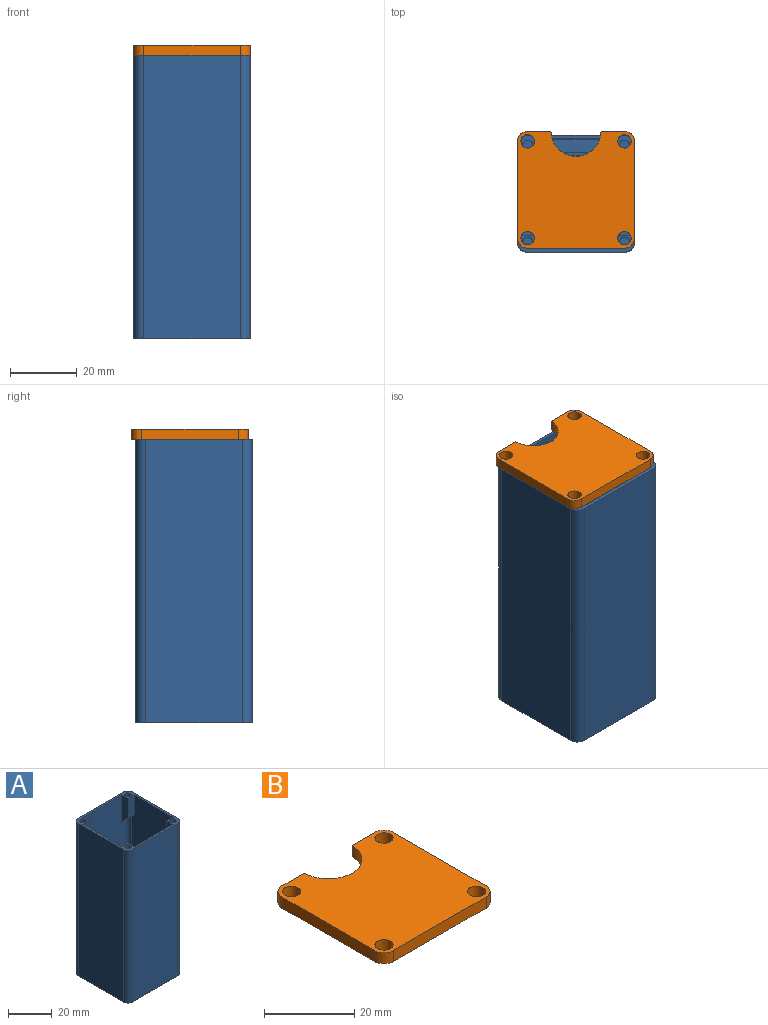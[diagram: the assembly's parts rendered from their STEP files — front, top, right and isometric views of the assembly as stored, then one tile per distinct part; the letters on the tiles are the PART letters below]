
ASSEMBLY  parts=2 mates=1
PART A: 41 faces, bbox 39.3x39.3x85.6 mm
  f0: plane 81x29mm, normal (0,-1,0), area 2289mm2, adj f4,f11,f22,f31,f35,f36,f37,f39
  f1: plane 81x29mm, normal (0,1,0), area 2289mm2, adj f4,f11,f25,f28,f33,f34,f38,f40
  f2: plane 81x29mm, normal (-1,0,0), area 2301mm2, adj f4,f11,f27,f30,f34,f36,f37,f38
  f3: plane 81x29mm, normal (1,0,0), area 2301mm2, adj f4,f11,f21,f24,f33,f35,f39,f40
  f4: plane 33x33mm, normal (0,0,1), area 460.6mm2, adj f0,f1,f2,f3,f16,f17,f18,f19
  f5: torus R=15mm, axis (0,0,1), area 344.5mm2, adj f10,f20
  f6: plane 85x29mm, normal (0,-1,0), area 2465mm2, adj f10,f11,f12,f15
  f7: plane 85x29mm, normal (1,0,0), area 2465mm2, adj f10,f11,f12,f13
  f8: plane 85x29mm, normal (0,1,0), area 2465mm2, adj f10,f11,f13,f14
  f9: plane 85x29mm, normal (-1,0,0), area 2465mm2, adj f10,f11,f14,f15
  f10: plane 35x35mm, normal (0,0,-1), area 510.4mm2, adj f5,f6,f7,f8,f9,f12,f13,f14
  f11: plane 35x35mm, normal (0,0,1), area 164mm2, adj f0,f1,f2,f3,f6,f7,f8,f9
  f12: cylinder r=3mm len=85mm, axis (0,0,1), area 400.6mm2, adj f6,f7,f10,f11
  f13: cylinder r=3mm len=85mm, axis (0,0,-1), area 400.6mm2, adj f7,f8,f10,f11
  f14: cylinder r=3mm len=85mm, axis (0,0,1), area 400.6mm2, adj f8,f9,f10,f11
  f15: cylinder r=3mm len=85mm, axis (0,0,-1), area 400.6mm2, adj f6,f9,f10,f11
  f16: plane 25x2mm, normal (0,1,0), area 50mm2, adj f4,f17,f19,f20
  f17: plane 25x2mm, normal (-1,0,0), area 50mm2, adj f4,f16,f18,f20
  f18: plane 25x2mm, normal (0,-1,0), area 50mm2, adj f4,f17,f19,f20
  f19: plane 25x2mm, normal (1,0,0), area 50mm2, adj f4,f16,f18,f20
  f20: plane 25x25mm, normal (0,0,1), area 206.9mm2, adj f5,f16,f17,f18,f19
  f21: plane 11x4mm, normal (0,-1,0), area 44mm2, adj f3,f11,f22,f35
  f22: plane 15x4mm, normal (1,0,0), area 52mm2, adj f0,f11,f21,f35
  f23: cylinder r=1.5mm len=14.51mm, axis (0,0,1), area 123mm2, adj f11,f35
  f24: plane 11x4mm, normal (0,1,0), area 44mm2, adj f3,f11,f25,f33
  f25: plane 15x4mm, normal (1,0,0), area 52mm2, adj f1,f11,f24,f33
  f26: cylinder r=1.5mm len=14.51mm, axis (0,0,1), area 123mm2, adj f11,f33
  f27: plane 11x4mm, normal (0,1,0), area 44mm2, adj f2,f11,f28,f34
  f28: plane 15x4mm, normal (-1,0,0), area 52mm2, adj f1,f11,f27,f34
  f29: cylinder r=1.5mm len=14.51mm, axis (0,0,1), area 123mm2, adj f11,f34
  f30: plane 11x4mm, normal (0,-1,0), area 44mm2, adj f2,f11,f31,f36
  f31: plane 15x4mm, normal (-1,0,0), area 52mm2, adj f0,f11,f30,f36
  f32: cylinder r=1.5mm len=14.51mm, axis (0,0,1), area 123mm2, adj f11,f36
  f33: plane 4.63x4.63mm, normal (0,0.71,-0.71), area 11.4mm2, adj f1,f3,f24,f25,f26,f40
  f34: plane 4.63x4.63mm, normal (0,0.71,-0.71), area 11.4mm2, adj f1,f2,f27,f28,f29,f38
  f35: plane 4.63x4.63mm, normal (0,-0.71,-0.71), area 11.4mm2, adj f0,f3,f21,f22,f23,f39
  f36: plane 4.63x4.63mm, normal (0,-0.71,-0.71), area 11.4mm2, adj f0,f2,f30,f31,f32,f37
  f37: cylinder r=2mm len=68mm, axis (0,0,1), area 209.6mm2, adj f0,f2,f4,f36
  f38: cylinder r=2mm len=68mm, axis (0,0,-1), area 209.6mm2, adj f1,f2,f4,f34
  f39: cylinder r=2mm len=68mm, axis (0,0,-1), area 209.6mm2, adj f0,f3,f4,f35
  f40: cylinder r=2mm len=68mm, axis (0,0,1), area 209.6mm2, adj f1,f3,f4,f33
PART B: 16 faces, bbox 35x35x3 mm
  f0: plane 7x3mm, normal (0,1,0), area 21mm2, adj f9,f10,f12,f15
  f1: plane 29x3mm, normal (0,-1,0), area 87mm2, adj f9,f10,f11,f14
  f2: plane 29x3mm, normal (1,0,0), area 87mm2, adj f9,f10,f11,f12
  f3: plane 7x3mm, normal (0,1,0), area 21mm2, adj f9,f10,f13,f15
  f4: cylinder r=2mm len=4mm, axis (0,0,-1), area 37.7mm2, adj f9,f10
  f5: cylinder r=2mm len=4mm, axis (0,0,-1), area 37.7mm2, adj f9,f10
  f6: cylinder r=2mm len=4mm, axis (0,0,-1), area 37.7mm2, adj f9,f10
  f7: cylinder r=2mm len=4mm, axis (0,0,-1), area 37.7mm2, adj f9,f10
  f8: plane 29x3mm, normal (-1,0,0), area 87mm2, adj f9,f10,f13,f14
  f9: plane 35x35mm, normal (0,0,1), area 1078.7mm2, adj f0,f1,f2,f3,f4,f5,f6,f7
  f10: plane 35x35mm, normal (0,0,-1), area 1078.7mm2, adj f0,f1,f2,f3,f4,f5,f6,f7
  f11: cylinder r=3mm len=3mm, axis (0,0,1), area 14.1mm2, adj f1,f2,f9,f10
  f12: cylinder r=3mm len=3mm, axis (0,0,-1), area 14.1mm2, adj f0,f2,f9,f10
  f13: cylinder r=3mm len=3mm, axis (0,0,1), area 14.1mm2, adj f3,f8,f9,f10
  f14: cylinder r=3mm len=3mm, axis (0,0,-1), area 14.1mm2, adj f1,f8,f9,f10
  f15: cylinder r=7.5mm len=15mm, axis (0,0,1), area 70.7mm2, adj f0,f3,f9,f10
PLACE A t=(-0.58,-1.07,-41.84)mm
PLACE B t=(-0.58,0.11,43.16)mm
MATE fastened B.f10 <-> A.f5  axis (0,0,-1) through (-0.58,-1.07,43.16)mm
